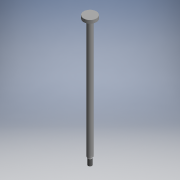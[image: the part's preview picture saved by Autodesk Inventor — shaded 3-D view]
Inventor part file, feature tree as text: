
AUTODESK INVENTOR PART (.ipt)
format: ipt  version: 2017.3 (Build 213256000, 256)  size: 129,536 bytes
history: native  units: mm (DEFAULTED — no unit token found)
features: other x28, sketch x3, revolve x2, thread x1, extrude x1
ambient origin geometry x8: Origin, YZ Plane, XZ Plane, XY Plane, X Axis, Y Axis, Z Axis, Center Point
bodies: Solid1 (feature_tree)
feature tree (35):
  revolve  "Revolution1"  Angle=360.0deg
  revolve  "Revolution2"  [1 undecoded]
  thread  "Thread1"  [1 undecoded]
  extrude  "Extrusion1"  [1 undecoded]
  other  "FDT_KSAUFSATZ_XY"
  other  "FDT_KSAUFSATZ_YZ"
  other  "FDT_KSAUFSATZ_ZX"
  other  "FDT_KSAUFSATZ_X"
  other  "FDT_KSAUFSATZ_Y"
  other  "FDT_KSAUFSATZ_Z"
  other  "FDT_KSAUFSATZ_Center"
  other  "FDT_NUT_XY"
  other  "FDT_NUT_YZ"
  other  "FDT_NUT_ZX"
  other  "FDT_NUT_X"
  other  "FDT_NUT_Y"
  other  "FDT_NUT_Z"
  other  "FDT_NUT_Center"
  other  "KS_XY"
  other  "KS_YZ"
  other  "KS_ZX"
  other  "KS_X"
  other  "KS_Y"
  other  "KS_Z"
  other  "KS_Center"
  other  "NUT1_XY"
  other  "NUT1_YZ"
  other  "NUT1_ZX"
  other  "NUT1_X"
  other  "NUT1_Y"
  other  "NUT1_Z"
  other  "NUT1_Center"
  sketch  "Sketch_2"  dims[d0=360.0deg d1=360.0deg]
  sketch  "Sketch_6"  dims[d2=19.2603mm d3=0.0mm d4=7.5mm d5=0.0mm]
  sketch  "Sketch_7"
note: 3 required parameter values undecoded (feature->parameter linkage not recoverable at this tier; creation-order binding heuristic only, values carry confidence <= 0.55)